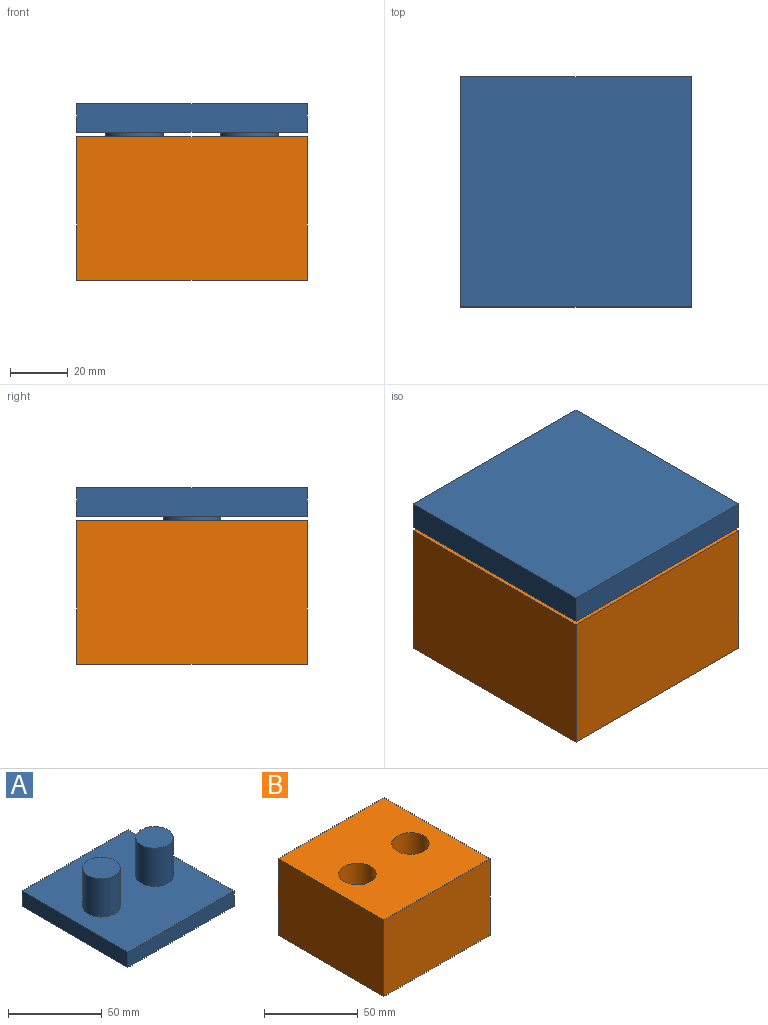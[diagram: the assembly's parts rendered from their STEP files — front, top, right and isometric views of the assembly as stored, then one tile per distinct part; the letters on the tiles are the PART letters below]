
ASSEMBLY  parts=2 mates=1
PART A: 10 faces, bbox 80x80x35 mm
  f0: plane 80x10mm, normal (0,-1,0), area 800mm2, adj f1,f3,f4,f5
  f1: plane 80x10mm, normal (1,0,0), area 800mm2, adj f0,f2,f4,f5
  f2: plane 80x10mm, normal (0,1,0), area 800mm2, adj f1,f3,f4,f5
  f3: plane 80x10mm, normal (-1,0,0), area 800mm2, adj f0,f2,f4,f5
  f4: plane 80x80mm, normal (0,0,1), area 5771.7mm2, adj f0,f1,f2,f3,f6,f8
  f5: plane 80x80mm, normal (0,0,-1), area 6400mm2, adj f0,f1,f2,f3
  f6: cylinder r=10mm len=25mm, axis (0,0,-1), area 1570.8mm2, adj f4,f7
  f7: plane 20x20mm, normal (0,0,1), area 314.2mm2, adj f6
  f8: cylinder r=10mm len=25mm, axis (0,0,-1), area 1570.8mm2, adj f4,f9
  f9: plane 20x20mm, normal (0,0,1), area 314.2mm2, adj f8
PART B: 10 faces, bbox 80x80x50 mm
  f0: plane 80x50mm, normal (0,-1,0), area 4000mm2, adj f1,f3,f4,f5
  f1: plane 80x50mm, normal (1,0,0), area 4000mm2, adj f0,f2,f4,f5
  f2: plane 80x50mm, normal (0,1,0), area 4000mm2, adj f1,f3,f4,f5
  f3: plane 80x50mm, normal (-1,0,0), area 4000mm2, adj f0,f2,f4,f5
  f4: plane 80x80mm, normal (0,0,1), area 5771.7mm2, adj f0,f1,f2,f3,f6,f8
  f5: plane 80x80mm, normal (0,0,-1), area 6400mm2, adj f0,f1,f2,f3
  f6: cylinder r=10mm len=25mm, axis (0,0,1), area 1570.8mm2, adj f4,f7
  f7: plane 20x20mm, normal (0,0,1), area 314.2mm2, adj f6
  f8: cylinder r=10mm len=25mm, axis (0,0,1), area 1570.8mm2, adj f4,f9
  f9: plane 20x20mm, normal (0,0,1), area 314.2mm2, adj f8
PLACE A rot(axis=(1,0,0),180deg) t=(-29.9,-17.01,36.8)mm
PLACE B t=(-29.9,-17.01,-24.62)mm fixed
MATE slider B.f8 <-> A.f6  axis (0,0,1) through (-49.9,-17.01,25.38)mm
